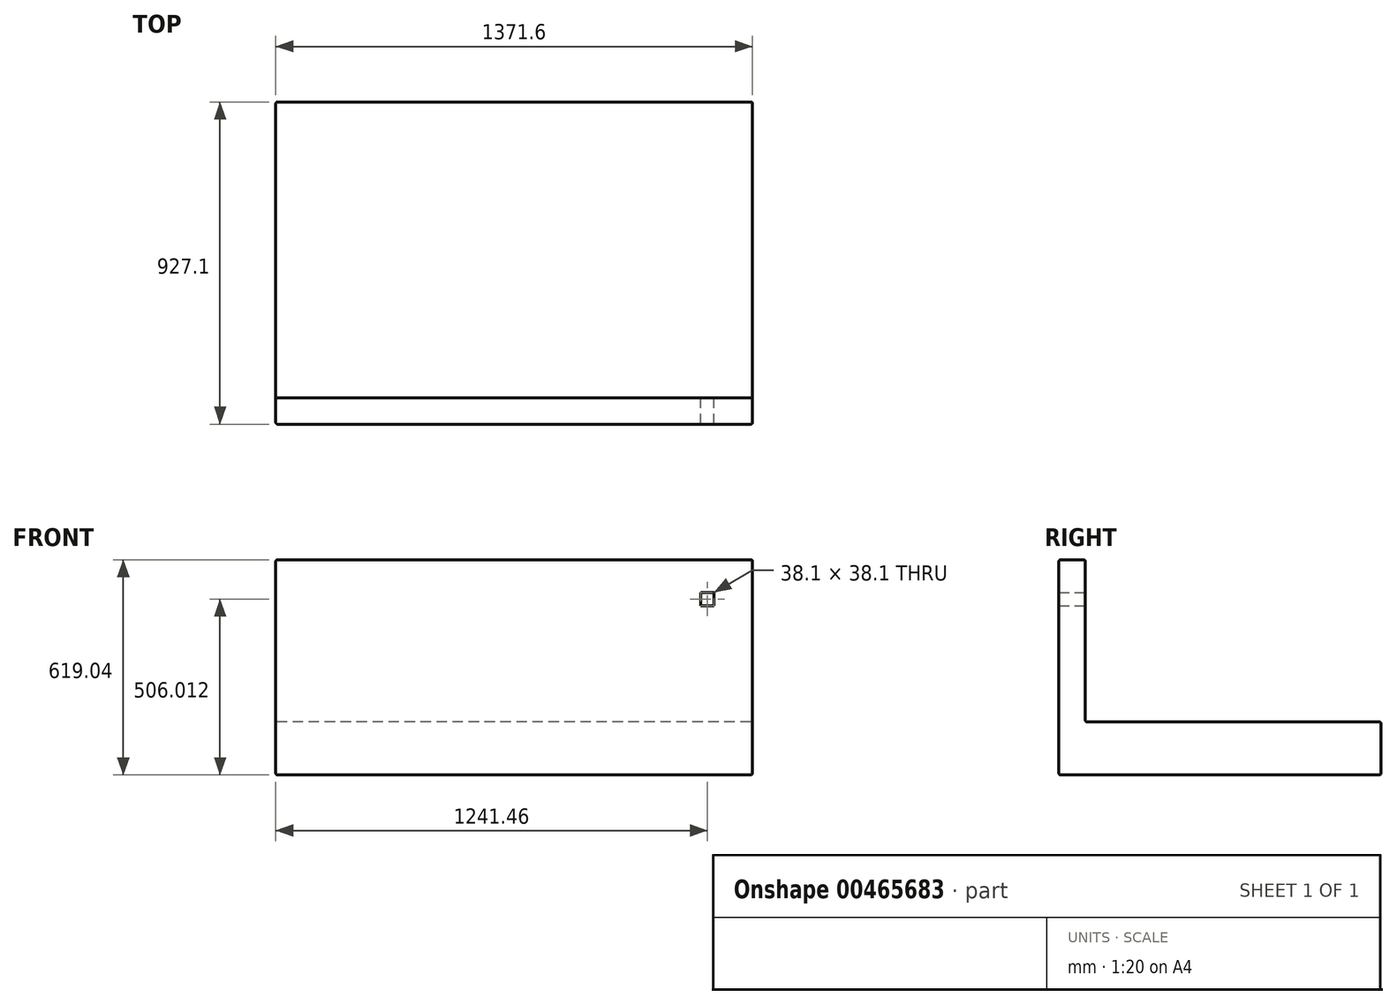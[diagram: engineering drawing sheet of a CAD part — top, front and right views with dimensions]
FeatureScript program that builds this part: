
annotation { "Feature Type Name" : "Feature", "Feature Type Description" : "" }
export const myFeature = defineFeature(function(context is Context, id is Id, definition is map)
    precondition{}
    {
        {
            var Q0;
            Q0=qCreatedBy(makeId("Right.planeOp"),FACE);
            var sketch = newSketch(context, id + "F0", { "sketchPlane" : qUnion([Q0])});
            skLineSegment(sketch, "E0.bottom", {"start": v(76.2, 47.73) * mm, "end": v(927.1, 47.73) * mm});
            skLineSegment(sketch, "E0.top", {"start": v(76.2, -104.67) * mm, "end": v(927.1, -104.67) * mm});
            skLineSegment(sketch, "E0.right", {"start": v(927.1, 47.73) * mm, "end": v(927.1, -104.67) * mm});
            skLineSegment(sketch, "E1.bottom", {"start": v(76.2, -104.67) * mm, "end": v(0, -104.67) * mm});
            skLineSegment(sketch, "E1.top", {"start": v(76.2, 514.37) * mm, "end": v(0, 514.37) * mm});
            skLineSegment(sketch, "E1.left", {"start": v(76.2, 47.73) * mm, "end": v(76.2, 514.37) * mm});
            skLineSegment(sketch, "E1.right", {"start": v(0, -104.67) * mm, "end": v(0, 514.37) * mm});
            skSolve(sketch);
        }
        {
            var Q0;
            Q0=makeQuery(id+"F0.imprint","IMPRINT",FACE,{"disambiguationData":[TD([[makeQuery(id+"F0.imprint","IMPRINT",EDGE,{"derivedFrom":sQuery(id+"F0.wireOp",EDGE,"E0.bottom")}),-1.0]])]});
            extrude(context, id + "F1", {"entities" : qUnion([Q0]), "endBound" : BoundingType.SYMMETRIC, "depth" : 1371.6 * mm});
        }
        {
            var Q0;
            Q0=makeQuery(id+"F1.opExtrude","SWEPT_EDGE",EDGE,{"disambiguationData":[OSD([sQuery(id+"F0.wireOp",EDGE,"E1.top"),sQuery(id+"F0.wireOp",EDGE,"E1.left")])]});
            var Q1;
            Q1=makeQuery(id+"F1.opExtrude","CAP_EDGE",EDGE,{"disambiguationData":[OSD([sQuery(id+"F0.wireOp",EDGE,"E1.left")])],"isStart":false});
            var Q2;
            Q2=makeQuery(id+"F1.opExtrude","CAP_EDGE",EDGE,{"disambiguationData":[OSD([sQuery(id+"F0.wireOp",EDGE,"E1.left")])],"isStart":true});
            var Q3;
            Q3=makeQuery(id+"F1.opExtrude","CAP_EDGE",EDGE,{"disambiguationData":[OSD([sQuery(id+"F0.wireOp",EDGE,"E0.bottom")])],"isStart":false});
            var Q4;
            Q4=makeQuery(id+"F1.opExtrude","SWEPT_EDGE",EDGE,{"disambiguationData":[OSD([sQuery(id+"F0.wireOp",EDGE,"E0.bottom"),sQuery(id+"F0.wireOp",EDGE,"E0.right")])]});
            var Q5;
            Q5=makeQuery(id+"F1.opExtrude","CAP_EDGE",EDGE,{"disambiguationData":[OSD([sQuery(id+"F0.wireOp",EDGE,"E0.bottom")])],"isStart":true});
            var Q6;
            Q6=makeQuery(id+"F1.opExtrude","SWEPT_FACE",FACE,{"disambiguationData":[OSD([sQuery(id+"F0.wireOp",EDGE,"E0.bottom")])]});
            var Q7;
            Q7=makeQuery(id+"F1.opExtrude","CAP_EDGE",EDGE,{"disambiguationData":[OSD([sQuery(id+"F0.wireOp",EDGE,"E0.right")])],"isStart":false});
            var Q8;
            Q8=makeQuery(id+"F1.opExtrude","SWEPT_FACE",FACE,{"disambiguationData":[OSD([sQuery(id+"F0.wireOp",EDGE,"E0.right")])]});
            var Q9;
            Q9=makeQuery(id+"F1.opExtrude","CAP_EDGE",EDGE,{"disambiguationData":[OSD([sQuery(id+"F0.wireOp",EDGE,"E0.right")])],"isStart":true});
            var Q10;
            Q10=makeQuery(id+"F1.opExtrude","SWEPT_EDGE",EDGE,{"disambiguationData":[OSD([sQuery(id+"F0.wireOp",EDGE,"E0.top"),sQuery(id+"F0.wireOp",EDGE,"E0.right")])]});
            var Q11;
            Q11=makeQuery(id+"F1.opExtrude","CAP_EDGE",EDGE,{"disambiguationData":[OSD([sQuery(id+"F0.wireOp",EDGE,"E0.top"),sQuery(id+"F0.wireOp",EDGE,"E1.bottom")])],"isStart":false});
            var Q12;
            Q12=makeQuery(id+"F1.opExtrude","CAP_EDGE",EDGE,{"disambiguationData":[OSD([sQuery(id+"F0.wireOp",EDGE,"E1.right")])],"isStart":false});
            var Q13;
            Q13=makeQuery(id+"F1.opExtrude","CAP_EDGE",EDGE,{"disambiguationData":[OSD([sQuery(id+"F0.wireOp",EDGE,"E1.top")])],"isStart":false});
            var Q14;
            Q14=makeQuery(id+"F1.opExtrude","SWEPT_EDGE",EDGE,{"disambiguationData":[OSD([sQuery(id+"F0.wireOp",EDGE,"E1.top"),sQuery(id+"F0.wireOp",EDGE,"E1.right")])]});
            var Q15;
            Q15=makeQuery(id+"F1.opExtrude","CAP_EDGE",EDGE,{"disambiguationData":[OSD([sQuery(id+"F0.wireOp",EDGE,"E1.top")])],"isStart":true});
            var Q16;
            Q16=makeQuery(id+"F1.opExtrude","CAP_EDGE",EDGE,{"disambiguationData":[OSD([sQuery(id+"F0.wireOp",EDGE,"E1.right")])],"isStart":true});
            var Q17;
            Q17=makeQuery(id+"F1.opExtrude","CAP_EDGE",EDGE,{"disambiguationData":[OSD([sQuery(id+"F0.wireOp",EDGE,"E0.top"),sQuery(id+"F0.wireOp",EDGE,"E1.bottom")])],"isStart":true});
            var Q18;
            Q18=makeQuery(id+"F1.opExtrude","CAP_FACE",FACE,{"disambiguationData":[OSD([sQuery(id+"F0.wireOp",EDGE,"E0.bottom"),sQuery(id+"F0.wireOp",EDGE,"E0.top"),sQuery(id+"F0.wireOp",EDGE,"E0.right"),sQuery(id+"F0.wireOp",EDGE,"E1.bottom"),sQuery(id+"F0.wireOp",EDGE,"E1.top"),sQuery(id+"F0.wireOp",EDGE,"E1.left"),sQuery(id+"F0.wireOp",EDGE,"E1.right")])],"isStart":true});
            var Q19;
            Q19=makeQuery(id+"F1.opExtrude","SWEPT_EDGE",EDGE,{"disambiguationData":[OSD([sQuery(id+"F0.wireOp",EDGE,"E1.bottom"),sQuery(id+"F0.wireOp",EDGE,"E1.right")])]});
            var Q20;
            Q20=makeQuery(id+"F1.opExtrude","SWEPT_FACE",FACE,{"disambiguationData":[OSD([sQuery(id+"F0.wireOp",EDGE,"E0.top"),sQuery(id+"F0.wireOp",EDGE,"E1.bottom")])]});
            fillet(context, id + "F2", {"entities" : qUnion([Q0, Q1, Q2, Q3, Q4, Q5, Q6, Q7, Q8, Q9, Q10, Q11, Q12, Q13, Q14, Q15, Q16, Q17, Q18, Q19, Q20]), "radius" : 5.08 * mm, "tangentPropagation" : true, "allowEdgeOverflow" : false});
        }
        {
            var Q0;
            Q0=makeQuery(id+"F1.opExtrude","SWEPT_FACE",FACE,{"disambiguationData":[OSD([sQuery(id+"F0.wireOp",EDGE,"E1.left")])]});
            var sketch = newSketch(context, id + "F3", { "sketchPlane" : qUnion([Q0])});
            skLineSegment(sketch, "E2.bottom", {"start": v(-596.9, 445.8) * mm, "end": v(591.82, 445.8) * mm});
            skLineSegment(sketch, "E2.top", {"start": v(-596.9, 179.8) * mm, "end": v(591.82, 179.8) * mm});
            skLineSegment(sketch, "E2.left", {"start": v(-622.3, 420.4) * mm, "end": v(-622.3, 205.2) * mm});
            skLineSegment(sketch, "E2.right", {"start": v(617.22, 420.4) * mm, "end": v(617.22, 205.2) * mm});
            skPoint(sketch, "E3.visualSharp", {"position": v(-622.3, 445.8) * mm});
            skArc(sketch, "E3.filletArc", {"start": v(-596.9, 445.8) * mm, "mid": v(-614.86, 438.35) * mm, "end": v(-622.3, 420.4) * mm});
            skPoint(sketch, "E4.visualSharp", {"position": v(-622.3, 179.8) * mm});
            skArc(sketch, "E4.filletArc", {"start": v(-622.3, 205.2) * mm, "mid": v(-614.86, 187.25) * mm, "end": v(-596.9, 179.8) * mm});
            skPoint(sketch, "E5.visualSharp", {"position": v(617.22, 445.8) * mm});
            skArc(sketch, "E5.filletArc", {"start": v(617.22, 420.4) * mm, "mid": v(609.78, 438.35) * mm, "end": v(591.82, 445.8) * mm});
            skPoint(sketch, "E6.visualSharp", {"position": v(617.22, 179.8) * mm});
            skArc(sketch, "E6.filletArc", {"start": v(591.82, 179.8) * mm, "mid": v(609.78, 187.25) * mm, "end": v(617.22, 205.2) * mm});
            skLineSegment(sketch, "E7.bottom", {"start": v(-574.71, 420.4) * mm, "end": v(-536.61, 420.4) * mm});
            skLineSegment(sketch, "E7.top", {"start": v(-574.71, 382.3) * mm, "end": v(-536.61, 382.3) * mm});
            skLineSegment(sketch, "E7.left", {"start": v(-574.71, 420.4) * mm, "end": v(-574.71, 382.3) * mm});
            skLineSegment(sketch, "E7.right", {"start": v(-536.61, 420.4) * mm, "end": v(-536.61, 382.3) * mm});
            skSolve(sketch);
        }
        {
            var Q0;
            Q0=makeQuery(id+"F3.imprint","IMPRINT",FACE,{"disambiguationData":[TD([[makeQuery(id+"F3.imprint","IMPRINT",EDGE,{"derivedFrom":sQuery(id+"F3.wireOp",EDGE,"E7.bottom")}),-1.0]])]});
            var Q1;
            Q1=makeQuery(id+"F1.opExtrude","SWEPT_FACE",FACE,{"disambiguationData":[OSD([sQuery(id+"F0.wireOp",EDGE,"E1.right")])]});
            extrude(context, id + "F4", {"entities" : qUnion([Q0, Q1]), "operationType" : NewBodyOperationType.REMOVE, "endBound" : BoundingType.THROUGH_ALL, "oppositeDirection" : true, "depth" : 25.4 * mm});
        }
    });
